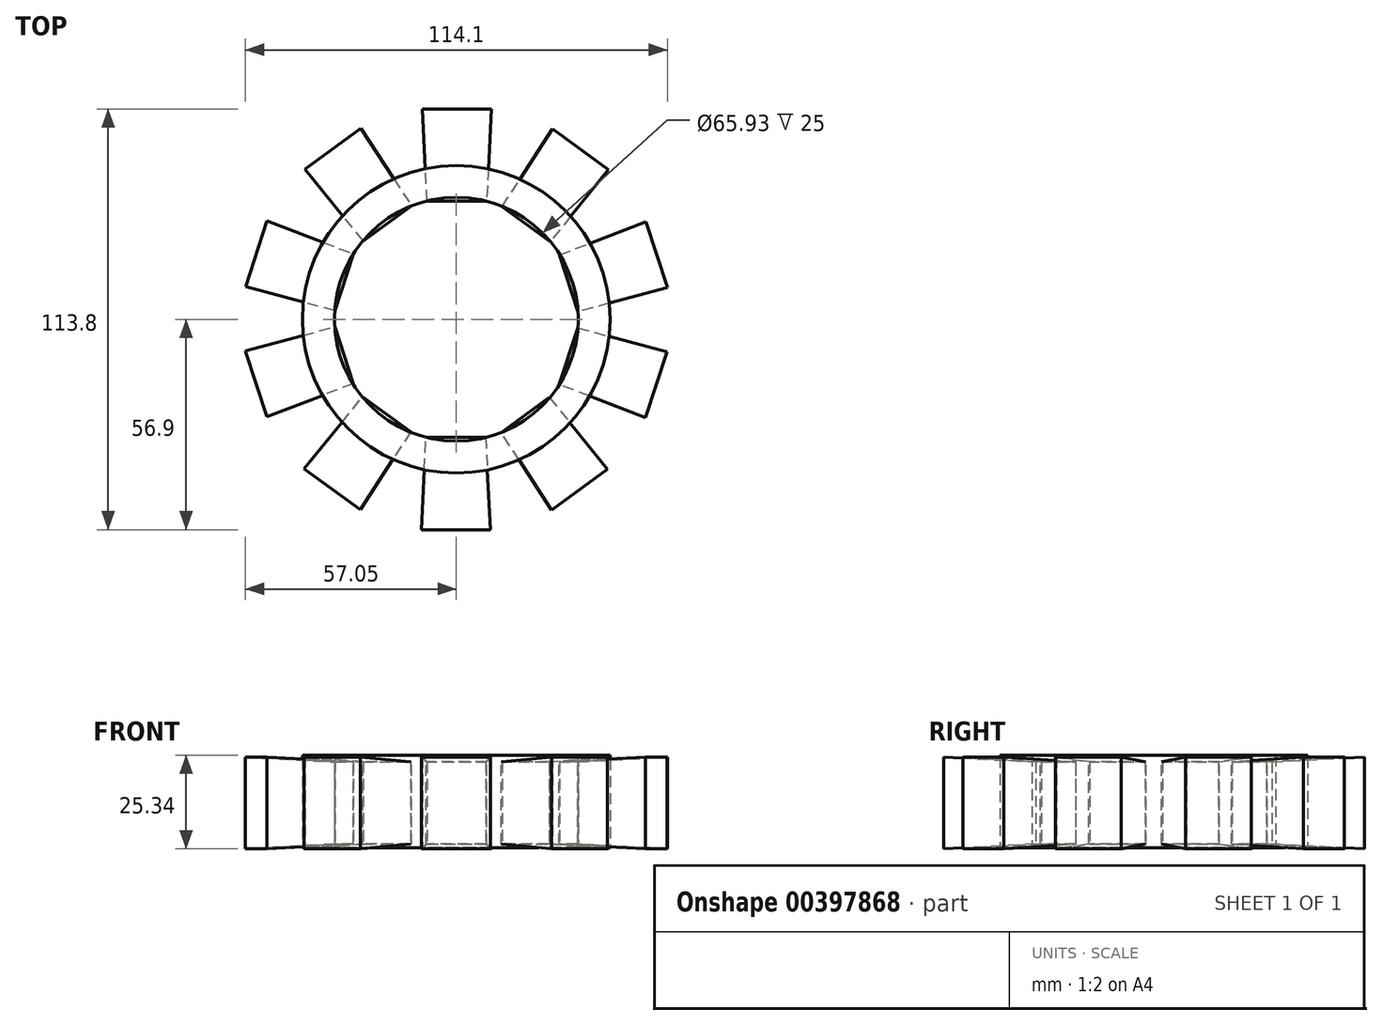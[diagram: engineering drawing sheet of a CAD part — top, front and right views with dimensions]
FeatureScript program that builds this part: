
annotation { "Feature Type Name" : "Feature", "Feature Type Description" : "" }
export const myFeature = defineFeature(function(context is Context, id is Id, definition is map)
    precondition{}
    {
        {
            var Q0;
            Q0=qCreatedBy(makeId("Top.planeOp"),FACE);
            var sketch = newSketch(context, id + "F0", { "sketchPlane" : qUnion([Q0])});
            skCircle(sketch, "E0", {"center": v(0, 0) * mm, "radius": 41.6 * mm});
            skCircle(sketch, "E1", {"center": v(0, 0) * mm, "radius": 32.97 * mm});
            skSolve(sketch);
        }
        {
            var Q0;
            Q0 = qSketchRegion(id + "F0", true);
            extrude(context, id + "F1", {"entities" : qUnion([Q0]), "depth" : 25 * mm});
        }
        {
            var Q0;
            Q0=qCreatedBy(makeId("Front.planeOp"),FACE);
            cPlane(context, id + "F2", {"entities" : qUnion([Q0]), "cplaneType" : CPlaneType.OFFSET, "offset" : 31.9 * mm, "oppositeDirection" : true, "width" : 150 * mm, "height" : 150 * mm});
        }
        {
            var Q0;
            Q0=qCreatedBy(id+"F2.planeOp",FACE);
            var sketch = newSketch(context, id + "F3", { "sketchPlane" : qUnion([Q0])});
            skLineSegment(sketch, "E2.bottom", {"start": v(-7.92, 23.2) * mm, "end": v(8.2, 23.2) * mm});
            skLineSegment(sketch, "E2.top", {"start": v(-7.92, 0.97) * mm, "end": v(8.2, 0.97) * mm});
            skLineSegment(sketch, "E2.left", {"start": v(-7.92, 23.2) * mm, "end": v(-7.92, 0.97) * mm});
            skLineSegment(sketch, "E2.right", {"start": v(8.2, 23.2) * mm, "end": v(8.2, 0.97) * mm});
            skSolve(sketch);
        }
        {
            var Q0;
            Q0 = qSketchRegion(id + "F3", true);
            extrude(context, id + "F4", {"entities" : qUnion([Q0]), "oppositeDirection" : true, "depth" : 25 * mm, "hasDraft" : true, "draftAngle" : 3 * degree});
        }
        {
            var Q0;
            Q0=makeQuery(id+"F4.opExtrude","SWEPT_BODY",BODY,{"disambiguationData":[OSD([sQuery(id+"F3.wireOp",EDGE,"E2.bottom"),sQuery(id+"F3.wireOp",EDGE,"E2.top"),sQuery(id+"F3.wireOp",EDGE,"E2.left"),sQuery(id+"F3.wireOp",EDGE,"E2.right")])]});
            var Q1;
            Q1=makeQuery(id+"F1.opExtrude","SWEPT_FACE",FACE,{"disambiguationData":[OSD([sQuery(id+"F0.wireOp",EDGE,"E0")])]});
            circularPattern(context, id + "F5", {"entities" : qUnion([Q0]), "axis" : qUnion([Q1]), "angle" : 360 * degree, "instanceCount" : 10, "equalSpace" : true});
        }
    });
